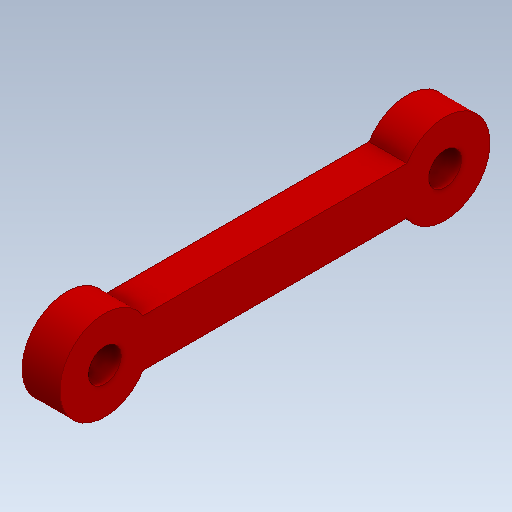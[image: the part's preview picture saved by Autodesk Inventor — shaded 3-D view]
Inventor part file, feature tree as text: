
AUTODESK INVENTOR PART (.ipt)
format: ipt  version: 2020 (Build 240168000, 168)  size: 120,320 bytes
history: native  units: in
note: dims shown in document units (in); Inventor stores cm internally (conversion verified against a paired STEP export)
features: extrude x1, sketch x1
ambient origin geometry x8: Origin, YZ Plane, XZ Plane, XY Plane, X Axis, Y Axis, Z Axis, Center Point
bodies: Solid1 (feature_tree)
feature tree (2):
  extrude  "Extrusion1"  Depth=1.4173in
  sketch  "Sketch1"  dims[d0=0.1378in d1=1.4173in d2=0.1181in d3=0.1181in d4=0.1969in d5=0.1575in d6=0.0in]
